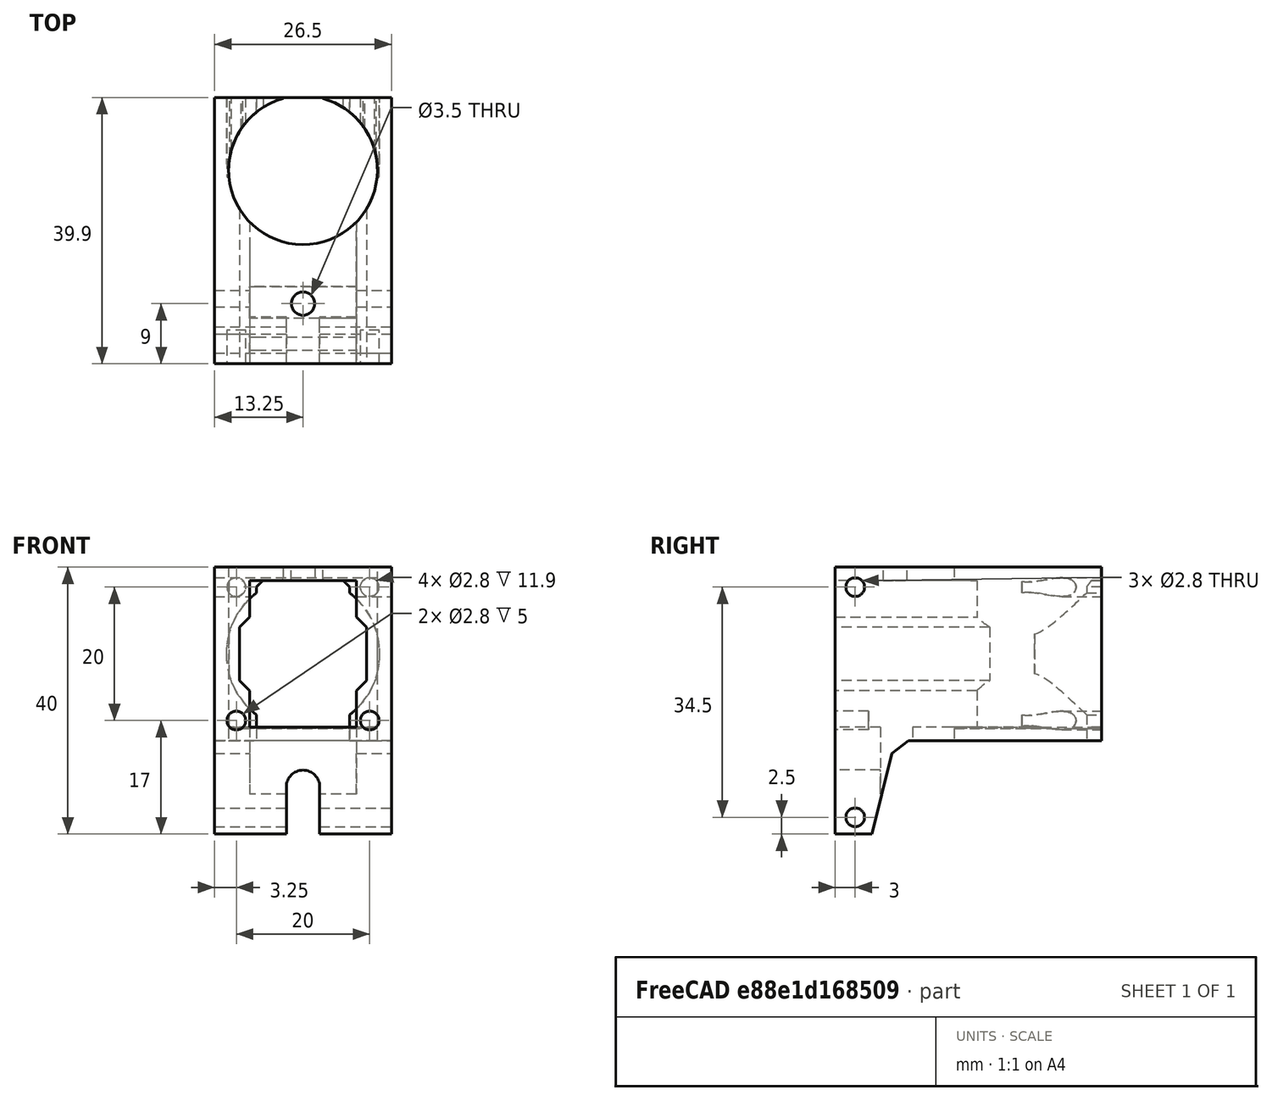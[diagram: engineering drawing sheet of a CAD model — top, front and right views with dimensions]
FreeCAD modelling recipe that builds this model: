
FCSTD DOCUMENT  (FreeCAD 0.19R)
Label: HSFBlock
License: All rights reserved
LicenseURL: http://en.wikipedia.org/wiki/All_rights_reserved
objects: Sketcher::SketchObject×15, PartDesign::Pocket×13, PartDesign::Pad×2, PartDesign::Chamfer×2, PartDesign::Body×1, Mesh::Feature×1
note: 50 computed .brp shape members not serialized (recipe doc carries the construction recipe); baked Part::Feature solids carry a one-line shape summary decoded from their .brp

FEATURE [Sketcher::SketchObject] Sketch
  FullyConstrained = true
  MapMode = 5
  Support = -> [XY_Plane]
  sketch-geometry (5):
    g0: LineSegment StartX=-13.25 StartY=10.9 StartZ=0 EndX=13.25 EndY=10.9 EndZ=0
    g1: LineSegment StartX=13.25 StartY=10.9 StartZ=0 EndX=13.25 EndY=-29 EndZ=0
    g2: LineSegment StartX=13.25 StartY=-29 StartZ=0 EndX=-13.25 EndY=-29 EndZ=0
    g3: LineSegment StartX=-13.25 StartY=-29 StartZ=0 EndX=-13.25 EndY=10.9 EndZ=0
    g4: Circle CenterX=0 CenterY=0 CenterZ=0 NormalX=0 NormalY=0 NormalZ=1 AngleXU=0 Radius=11
  constraints (12):
    c: Distance(g0) = 26.5
    c: Symmetric(g0,g0,g-2)
    c: DistanceY(g0) = 10.9
    c: Coincident(g1,g2)
    c: Coincident(g2,g3)
    c: Symmetric(g1,g2,g-2)
    c: Distance(g2) = 26.5
    c: DistanceY(g1) = -29
    c: Coincident(g4,g-1)
    c: Diameter(g4) = 22
    c: Coincident(g3,g0)
    c: Coincident(g1,g0)
FEATURE [PartDesign::Pad] Pad
  Direction = (1,1,1)
  Length = 26
  Length2 = 14
  Profile = -> Sketch
  Type = 4
FEATURE [Sketcher::SketchObject] Sketch002  label="25mmFanHoles"
  FullyConstrained = true
  MapMode = 5
  Placement = pos=(0,15,0) rot=(0,0.707107,0.707107;3.14159rad)
  sketch-geometry (4):
    g0: Circle CenterX=-10 CenterY=23 CenterZ=0 NormalX=0 NormalY=0 NormalZ=1 AngleXU=0 Radius=1.4
    g1: Circle CenterX=10 CenterY=23 CenterZ=0 NormalX=0 NormalY=0 NormalZ=1 AngleXU=0 Radius=1.4
    g2: Circle CenterX=-10 CenterY=3 CenterZ=0 NormalX=0 NormalY=0 NormalZ=1 AngleXU=0 Radius=1.4
    g3: Circle CenterX=10 CenterY=3 CenterZ=0 NormalX=0 NormalY=0 NormalZ=1 AngleXU=0 Radius=1.4
  constraints (10):
    c: Diameter(g1) = 2.8
    c: Equal(g1,g2)
    c: Equal(g1,g3)
    c: Equal(g1,g0)
    c: Symmetric(g3,g2,g-2)
    c: Distance(g3,g2) = 20
    c: Symmetric(g1,g0,g-2)
    c: Distance(g1,g0) = 20
    c: Distance(g3,g1) = 20
    c: DistanceY(g3) = 3
FEATURE [Sketcher::SketchObject] Sketch003  label="FrontHole"
  FullyConstrained = false
  MapMode = 5
  Placement = pos=(0,15,0) rot=(0,0.707107,0.707107;3.14159rad)
  sketch-geometry (13):
    g0: LineSegment StartX=-7 StartY=24 StartZ=0 EndX=7 EndY=24 EndZ=0
    g1: LineSegment StartX=7.1367 StartY=-2.22646 StartZ=0 EndX=-7.1367 EndY=-2.22646 EndZ=0
    g2: LineSegment StartX=-7 StartY=24 StartZ=0 EndX=-7 EndY=19.5 EndZ=0
    g3: LineSegment StartX=-7 StartY=19.5 StartZ=0 EndX=-9.5 EndY=17 EndZ=0
    g4: LineSegment StartX=-9.5 StartY=17 StartZ=0 EndX=-9.5 EndY=9 EndZ=0
    g5: LineSegment StartX=-9.5 StartY=9 StartZ=0 EndX=-7 EndY=6.5 EndZ=0
    g6: LineSegment StartX=-7 StartY=6.5 StartZ=0 EndX=-7 EndY=2 EndZ=0
    g7: LineSegment StartX=-7 StartY=2 StartZ=0 EndX=7 EndY=2 EndZ=0
    g8: LineSegment StartX=7 StartY=2 StartZ=0 EndX=7 EndY=6.5 EndZ=0
    g9: LineSegment StartX=7 StartY=6.5 StartZ=0 EndX=9.5 EndY=9 EndZ=0
    g10: LineSegment StartX=9.5 StartY=9 StartZ=0 EndX=9.5 EndY=17 EndZ=0
    g11: LineSegment StartX=9.5 StartY=17 StartZ=0 EndX=7 EndY=19.5 EndZ=0
    g12: LineSegment StartX=7 StartY=19.5 StartZ=0 EndX=7 EndY=24 EndZ=0
  constraints (32):
    c: Symmetric(g1,g1,g-2)
    c: DistanceY(g0) = 24
    c: Coincident(g0,g2)
    c: Vertical(g2)
    c: Coincident(g2,g3)
    c: Coincident(g3,g4)
    c: Vertical(g4)
    c: Coincident(g4,g5)
    c: Coincident(g5,g6)
    c: Vertical(g6)
    c: Coincident(g6,g7)
    c: Coincident(g7,g8)
    c: Coincident(g8,g9)
    c: Coincident(g9,g10)
    c: Vertical(g10)
    c: Coincident(g10,g11)
    c: Coincident(g11,g12)
    c: Coincident(g12,g0)
    c: Symmetric(g0,g0,g-2)
    c: Distance(g0) = 14
    c: Equal(g7,g0)
    c: Symmetric(g7,g6,g-2)
    c: Symmetric(g8,g5,g-2)
    c: Symmetric(g11,g2,g-2)
    c: Equal(g3,g5)
    c: Equal(g5,g9)
    c: Symmetric(g10,g3,g-2)
    c: Distance(g4,g9) = 19
    c: Distance(g10) = 8
    c: Equal(g8,g12)
    c: DistanceY(g7) = 2
    c: Angle(g3) = -2.35619
FEATURE [Sketcher::SketchObject] Sketch006  label="HeatSinkRoundHole"
  FullyConstrained = true
  MapMode = 5
  Placement = pos=(0,0,-14) rot=(1,0,0;3.14159rad)
  Support = -> [Pad]
  sketch-geometry (1):
    g0: Circle CenterX=0 CenterY=0 CenterZ=0 NormalX=0 NormalY=0 NormalZ=1 AngleXU=0 Radius=11.15
  constraints (2):
    c: Coincident(g0,g-1)
    c: Diameter(g0) = 22.3
FEATURE [PartDesign::Pocket] Pocket
  BaseFeature = -> Pad
  Length = 5
  Length2 = 100
  Profile = -> Sketch006
  Type = 1
FEATURE [PartDesign::Pocket] Pocket001
  BaseFeature = -> Pocket
  Length = 5
  Length2 = 100
  Profile = -> Sketch003
  Type = 1
FEATURE [Sketcher::SketchObject] Sketch007  label="FrontTrim"
  FullyConstrained = false
  MapMode = 5
  Placement = pos=(0,0,26) rot=(0,0,1;0rad)
  Support = -> [Pocket001]
  sketch-geometry (4):
    g0: LineSegment StartX=-3 StartY=15.8374 StartZ=0 EndX=3 EndY=15.8374 EndZ=0
    g1: LineSegment StartX=3 StartY=15.8374 StartZ=0 EndX=3 EndY=5.98993 EndZ=0
    g2: LineSegment StartX=3 StartY=5.98993 StartZ=0 EndX=-3 EndY=5.98993 EndZ=0
    g3: LineSegment StartX=-3 StartY=5.98993 StartZ=0 EndX=-3 EndY=15.8374 EndZ=0
  constraints (9):
    c: Coincident(g0,g1)
    c: Coincident(g1,g2)
    c: Coincident(g2,g3)
    c: Coincident(g3,g0)
    c: Horizontal(g2)
    c: Vertical(g1)
    c: Vertical(g3)
    c: Distance(g0) = 6
    c: Symmetric(g0,g0,g-2)
FEATURE [PartDesign::Pocket] Pocket002
  BaseFeature = -> Pocket001
  Length = 5
  Length2 = 100
  Profile = -> Sketch007
  Type = 0
FEATURE [PartDesign::Pocket] Pocket003
  BaseFeature = -> Pocket002
  Length = 16
  Length2 = 100
  Profile = -> Sketch002
  Type = 0
FEATURE [Sketcher::SketchObject] Sketch009  label="SideNotchB"
  FullyConstrained = true
  MapMode = 5
  Placement = pos=(-13.25,0,0) rot=(0.57735,-0.57735,-0.57735;2.0944rad)
  Support = -> [Pocket003]
  sketch-geometry (4):
    g0: LineSegment StartX=-15.9544 StartY=0 StartZ=0 EndX=20 EndY=0 EndZ=0
    g1: LineSegment StartX=25 StartY=-20 StartZ=0 EndX=-15.9544 EndY=-20 EndZ=0
    g2: LineSegment StartX=-15.9544 StartY=-20 StartZ=0 EndX=-15.9544 EndY=0 EndZ=0
    g3: LineSegment StartX=20 StartY=0 StartZ=0 EndX=25 EndY=-20 EndZ=0
  constraints (12):
    c: Coincident(g1,g2)
    c: Coincident(g2,g0)
    c: Horizontal(g0)
    c: Horizontal(g1)
    c: Vertical(g2)
    c: PointOnObject(g0,g-1)
    c: DistanceY(g1) = -20
    c: DistanceX(g1) = 25
    c: Coincident(g3,g0)
    c: Coincident(g3,g1)
    c: DistanceX(g0) = 20
    c: DistanceX(g1) = -15.9544
FEATURE [Sketcher::SketchObject] Sketch010  label="topTrim"
  FullyConstrained = false
  MapMode = 5
  Placement = pos=(0,0,-14) rot=(1,0,0;3.14159rad)
  sketch-geometry (4):
    g0: LineSegment StartX=-7 StartY=-6.16385 StartZ=0 EndX=7 EndY=-6.16385 EndZ=0
    g1: LineSegment StartX=7 StartY=-6.16385 StartZ=0 EndX=7 EndY=-16.9205 EndZ=0
    g2: LineSegment StartX=7 StartY=-16.9205 StartZ=0 EndX=-7 EndY=-16.9205 EndZ=0
    g3: LineSegment StartX=-7 StartY=-16.9205 StartZ=0 EndX=-7 EndY=-6.16385 EndZ=0
  constraints (9):
    c: Coincident(g0,g1)
    c: Coincident(g1,g2)
    c: Coincident(g2,g3)
    c: Coincident(g3,g0)
    c: Horizontal(g2)
    c: Vertical(g1)
    c: Vertical(g3)
    c: Distance(g0) = 14
    c: Symmetric(g0,g0,g-2)
FEATURE [Sketcher::SketchObject] Sketch011  label="MountHole"
  FullyConstrained = true
  MapMode = 5
  Placement = pos=(0,0,26) rot=(0,0,1;0rad)
  sketch-geometry (1):
    g0: Circle CenterX=0 CenterY=-20 CenterZ=0 NormalX=0 NormalY=0 NormalZ=1 AngleXU=0 Radius=1.75
  constraints (3):
    c: PointOnObject(g0,g-2)
    c: Diameter(g0) = 3.5
    c: DistanceY(g0) = -20
FEATURE [PartDesign::Pocket] Pocket004
  BaseFeature = -> Pocket003
  Length = 5
  Length2 = 100
  Profile = -> Sketch009
  Type = 1
FEATURE [PartDesign::Pocket] Pocket005
  BaseFeature = -> Pocket004
  Length = 18
  Length2 = 100
  Profile = -> Sketch010
  Type = 0
FEATURE [PartDesign::Pocket] Pocket006
  BaseFeature = -> Pocket005
  Length = 5
  Length2 = 100
  Profile = -> Sketch011
  Type = 1
FEATURE [Sketcher::SketchObject] Sketch012  label="InnerTrim"
  FullyConstrained = true
  MapMode = 5
  Placement = pos=(4e-16,-1,1e-15) rot=(0,0.707107,0.707107;3.14159rad)
  Support = -> [Pocket006]
  sketch-geometry (4):
    g0: LineSegment StartX=-8 StartY=24 StartZ=0 EndX=8 EndY=24 EndZ=0
    g1: LineSegment StartX=8 StartY=24 StartZ=0 EndX=8 EndY=2 EndZ=0
    g2: LineSegment StartX=8 StartY=2 StartZ=0 EndX=-8 EndY=2 EndZ=0
    g3: LineSegment StartX=-8 StartY=2 StartZ=0 EndX=-8 EndY=24 EndZ=0
  constraints (11):
    c: Coincident(g0,g1)
    c: Coincident(g1,g2)
    c: Coincident(g2,g3)
    c: Coincident(g3,g0)
    c: Horizontal(g2)
    c: Vertical(g1)
    c: Vertical(g3)
    c: DistanceY(g1) = 2
    c: DistanceY(g0) = 24
    c: Symmetric(g0,g0,g-2)
    c: Distance(g2) = 16
FEATURE [PartDesign::Pocket] Pocket007
  BaseFeature = -> Pocket006
  Length = 5
  Length2 = 100
  Profile = -> Sketch012
  Type = 1
FEATURE [Sketcher::SketchObject] Sketch013  label="RearFanHoles"
  FullyConstrained = true
  MapMode = 5
  Placement = pos=(0,-29,0) rot=(1,0,0;1.5708rad)
  Support = -> [Pocket007]
  sketch-geometry (4):
    g0: Circle CenterX=-10 CenterY=23 CenterZ=0 NormalX=0 NormalY=0 NormalZ=1 AngleXU=0 Radius=1.4
    g1: Circle CenterX=10 CenterY=23 CenterZ=0 NormalX=0 NormalY=0 NormalZ=1 AngleXU=0 Radius=1.4
    g2: Circle CenterX=-10 CenterY=3 CenterZ=0 NormalX=0 NormalY=0 NormalZ=1 AngleXU=0 Radius=1.4
    g3: Circle CenterX=10 CenterY=3 CenterZ=0 NormalX=0 NormalY=0 NormalZ=1 AngleXU=0 Radius=1.4
  constraints (10):
    c: Diameter(g0) = 2.8
    c: Equal(g0,g1)
    c: Equal(g0,g2)
    c: Equal(g0,g3)
    c: Symmetric(g1,g0,g-2)
    c: Distance(g1,g0) = 20
    c: Symmetric(g3,g2,g-2)
    c: Distance(g2,g3) = 20
    c: Distance(g1,g3) = 20
    c: DistanceY(g3) = 3
FEATURE [PartDesign::Pocket] Pocket008
  BaseFeature = -> Pocket007
  Length = 5
  Length2 = 100
  Profile = -> Sketch013
  Type = 0
FEATURE [Sketcher::SketchObject] Sketch004  label="BlowerHoles"
  FullyConstrained = true
  MapMode = 5
  Placement = pos=(13.25,0,0) rot=(0.57735,0.57735,0.57735;2.0944rad)
  Support = -> [Pocket008]
  sketch-geometry (8):
    g0: Circle CenterX=-26 CenterY=23 CenterZ=0 NormalX=0 NormalY=0 NormalZ=1 AngleXU=0 Radius=1.4
    g1: Circle CenterX=8 CenterY=23 CenterZ=0 NormalX=0 NormalY=0 NormalZ=1 AngleXU=0 Radius=1.4
    g2: Circle CenterX=-26 CenterY=-11.5 CenterZ=0 NormalX=0 NormalY=0 NormalZ=1 AngleXU=0 Radius=1.4
    g3: Circle CenterX=8 CenterY=-11.5 CenterZ=0 NormalX=0 NormalY=0 NormalZ=1 AngleXU=0 Radius=3.285
    g4: LineSegment StartX=-26 StartY=23 StartZ=0 EndX=8 EndY=23 EndZ=0
    g5: LineSegment StartX=8 StartY=23 StartZ=0 EndX=8 EndY=-11.5 EndZ=0
    g6: LineSegment StartX=8 StartY=-11.5 StartZ=0 EndX=-26 EndY=-11.5 EndZ=0
    g7: LineSegment StartX=-26 StartY=-11.5 StartZ=0 EndX=-26 EndY=23 EndZ=0
  constraints (20):
    c: Coincident(g4,g0)
    c: Coincident(g4,g1)
    c: Coincident(g4,g5)
    c: Coincident(g5,g3)
    c: Vertical(g5)
    c: Coincident(g5,g6)
    c: Coincident(g6,g2)
    c: Horizontal(g6)
    c: Coincident(g6,g7)
    c: Coincident(g7,g4)
    c: Vertical(g7)
    c: Diameter(g0) = 2.8
    c: DistanceY(g1) = 23
    c: DistanceY(g0) = 23
    c: DistanceX(g1) = 8
    c: DistanceY(g2) = -11.5
    c: DistanceX(g0) = -26
    c: Diameter(g2) = 2.8
    c: Diameter(g3) = 6.57
    c: Diameter(g1) = 2.8
FEATURE [PartDesign::Pocket] Pocket009
  BaseFeature = -> Pocket008
  Length = 5
  Length2 = 100
  Profile = -> Sketch004
  Type = 1
FEATURE [Sketcher::SketchObject] Sketch014
  FullyConstrained = false
  MapMode = 5
  Placement = pos=(0,4e-16,2) rot=(0,0,1;0rad)
  Support = -> [Pocket009]
  sketch-geometry (4):
    g0: LineSegment StartX=-8 StartY=-17.4209 StartZ=0 EndX=8 EndY=-17.4209 EndZ=0
    g1: LineSegment StartX=8 StartY=-17.4209 StartZ=0 EndX=8 EndY=-22.2311 EndZ=0
    g2: LineSegment StartX=8 StartY=-22.2311 StartZ=0 EndX=-8 EndY=-22.2311 EndZ=0
    g3: LineSegment StartX=-8 StartY=-22.2311 StartZ=0 EndX=-8 EndY=-17.4209 EndZ=0
  constraints (9):
    c: Coincident(g0,g1)
    c: Coincident(g1,g2)
    c: Coincident(g2,g3)
    c: Coincident(g3,g0)
    c: Horizontal(g2)
    c: Vertical(g1)
    c: Vertical(g3)
    c: Distance(g0) = 16
    c: Symmetric(g0,g0,g-2)
FEATURE [PartDesign::Pocket] Pocket010
  BaseFeature = -> Pocket009
  Length = 10
  Length2 = 100
  Profile = -> Sketch014
  Type = 0
FEATURE [Sketcher::SketchObject] Sketch015  label="printfilm"
  FullyConstrained = false
  MapMode = 5
  Placement = pos=(0,4e-16,2) rot=(0,0,1;0rad)
  Support = -> [Pocket010]
  sketch-geometry (4):
    g0: LineSegment StartX=-11.4529 StartY=10.8853 StartZ=0 EndX=11.6797 EndY=10.8853 EndZ=0
    g1: LineSegment StartX=11.6797 StartY=10.8853 StartZ=0 EndX=11.6797 EndY=-11.5315 EndZ=0
    g2: LineSegment StartX=11.6797 StartY=-11.5315 StartZ=0 EndX=-11.4529 EndY=-11.5315 EndZ=0
    g3: LineSegment StartX=-11.4529 StartY=-11.5315 StartZ=0 EndX=-11.4529 EndY=10.8853 EndZ=0
  constraints (8):
    c: Coincident(g0,g1)
    c: Coincident(g1,g2)
    c: Coincident(g2,g3)
    c: Coincident(g3,g0)
    c: Horizontal(g0)
    c: Horizontal(g2)
    c: Vertical(g1)
    c: Vertical(g3)
FEATURE [Sketcher::SketchObject] Sketch016
  ExternalGeometry = -> [Pocket005]
  FullyConstrained = true
  MapMode = 5
  Placement = pos=(-7e-16,10.9,0) rot=(0,0.707107,0.707107;3.14159rad)
  Support = -> [Pocket005]
  sketch-geometry (1):
    g0: Circle CenterX=-1e-16 CenterY=13 CenterZ=0 NormalX=0 NormalY=0 NormalZ=1 AngleXU=0 Radius=11.5
  constraints (2):
    c: Symmetric(g-4,g-3,g0)
    c: Diameter(g0) = 23
FEATURE [PartDesign::Pocket] Pocket011
  BaseFeature = -> Pocket010
  Length = 10
  Length2 = 100
  Profile = -> Sketch016
  Type = 0
FEATURE [PartDesign::Pad] Pad001
  BaseFeature = -> Pocket011
  Direction = (1,1,1)
  Length = 0.2
  Length2 = 100
  Profile = -> Sketch015
  Reversed = true
  Type = 0
FEATURE [Sketcher::SketchObject] Sketch018
  FullyConstrained = false
  MapMode = 5
  Placement = pos=(0,-29,0) rot=(1,0,0;1.5708rad)
  Support = -> [Pad001]
  sketch-geometry (4):
    g0: ArcOfCircle CenterX=0 CenterY=-6.93311 CenterZ=0 NormalX=0 NormalY=0 NormalZ=1 AngleXU=0 Radius=2.5 StartAngle=1e-16 EndAngle=3.14159
    g1: ArcOfCircle CenterX=0 CenterY=-15.2954 CenterZ=0 NormalX=0 NormalY=0 NormalZ=1 AngleXU=0 Radius=2.5 StartAngle=3.14159 EndAngle=6.28319
    g2: LineSegment StartX=-2.5 StartY=-6.93311 StartZ=0 EndX=-2.5 EndY=-15.2954 EndZ=0
    g3: LineSegment StartX=2.5 StartY=-6.93311 StartZ=0 EndX=2.5 EndY=-15.2954 EndZ=0
  constraints (8):
    c: Tangent(g0,g3) = 1.5708
    c: Tangent(g0,g2) = -1.5708
    c: Tangent(g2,g1) = -1.5708
    c: Tangent(g3,g1) = 1.5708
    c: Vertical(g2)
    c: Equal(g0,g1)
    c: PointOnObject(g0,g-2)
    c: Distance(g0,g0) = 5
FEATURE [PartDesign::Pocket] Pocket012
  BaseFeature = -> Pad001
  Length = 9
  Length2 = 100
  Profile = -> Sketch018
  Type = 0
FEATURE [PartDesign::Chamfer] Chamfer
  Angle = 45
  Base = -> Pocket012 [Edge50,Edge46]
  BaseFeature = -> Pocket012
  ChamferType = 0
  FlipDirection = false
  Size = 2
  Size2 = 1
  SupportTransform = false
FEATURE [PartDesign::Chamfer] Chamfer001
  Angle = 45
  Base = -> Chamfer [Edge272,Edge190]
  BaseFeature = -> Chamfer
  ChamferType = 0
  FlipDirection = false
  Size = 1
  Size2 = 1
  SupportTransform = false
FEATURE [PartDesign::Body] Body
  Group = -> [Sketch,Pad,Sketch002,Sketch003,Sketch004,Sketch006,Pocket,Pocket001,Sketch007,Pocket002,Pocket003,Sketch009,Sketch010,Sketch011,Pocket004,Pocket005,Pocket006,Sketch012,Pocket007,Sketch013,Pocket008,Pocket009,Sketch014,Pocket010,Sketch015,Sketch016,Pocket011,Pad001,Sketch018,Pocket012,Chamfer,Chamfer001]
  Origin = -> Origin
  Tip = -> Chamfer001
FEATURE [Mesh::Feature] Mesh  label="Chamfer001 (Meshed)"
